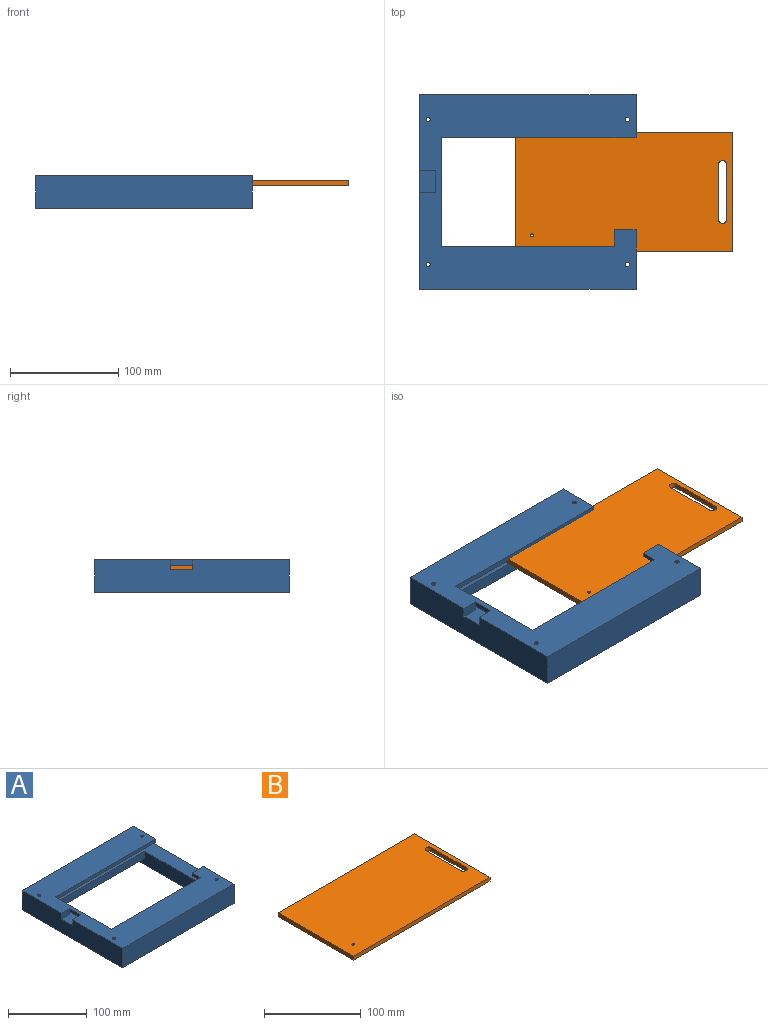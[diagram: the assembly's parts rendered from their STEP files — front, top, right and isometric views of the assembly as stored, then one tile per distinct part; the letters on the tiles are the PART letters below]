
ASSEMBLY  parts=2 mates=2
PART A: 32 faces, bbox 200x180x30 mm
  f0: plane 54.46x4mm, normal (1,0,0), area 217.8mm2, adj f3,f24,f25,f30
  f1: plane 200x180mm, normal (0,0,1), area 17949.7mm2, adj f2,f4,f5,f6,f7,f11,f12,f13
  f2: plane 180x30mm, normal (1,0,0), area 4535mm2, adj f1,f3,f4,f10,f11,f13,f24,f25
  f3: plane 185x110mm, normal (0,0,-1), area 2650mm2, adj f0,f2,f4,f5,f6,f7,f25,f26
  f4: plane 180x5mm, normal (0,-1,0), area 900mm2, adj f1,f2,f3,f6
  f5: plane 160x5mm, normal (0,1,0), area 800mm2, adj f1,f3,f6,f7
  f6: plane 100x5mm, normal (1,0,0), area 500mm2, adj f1,f3,f4,f5
  f7: plane 15x5mm, normal (-1,0,0), area 75mm2, adj f1,f3,f5,f28
  f8: plane 160x11mm, normal (0,-1,0), area 1760mm2, adj f14,f15,f23,f24
  f9: plane 160x11mm, normal (0,1,0), area 1760mm2, adj f14,f15,f20,f24
  f10: plane 200x180mm, normal (0,0,-1), area 10349.7mm2, adj f2,f11,f12,f13,f14,f15,f16,f17
  f11: plane 200x30mm, normal (0,1,0), area 6000mm2, adj f1,f2,f10,f12
  f12: plane 180x30mm, normal (-1,0,0), area 5220mm2, adj f1,f10,f11,f13,f24,f29,f30
  f13: plane 200x30mm, normal (0,-1,0), area 6000mm2, adj f1,f2,f10,f12
  f14: plane 160x21mm, normal (1,0,0), area 2700mm2, adj f8,f9,f10,f20,f21,f22,f23,f24
  f15: plane 160x21mm, normal (-1,0,0), area 2700mm2, adj f8,f9,f10,f20,f21,f22,f23,f24
  f16: cylinder r=2mm len=30mm, axis (0,0,1), area 377mm2, adj f1,f10
  f17: cylinder r=2mm len=30mm, axis (0,0,1), area 377mm2, adj f1,f10
  f18: cylinder r=2mm len=30mm, axis (0,0,1), area 377mm2, adj f1,f10
  f19: cylinder r=2mm len=30mm, axis (0,0,1), area 377mm2, adj f1,f10
  f20: plane 160x30mm, normal (0,0,-1), area 4800mm2, adj f9,f14,f15,f21
  f21: plane 160x10mm, normal (0,1,0), area 1600mm2, adj f10,f14,f15,f20
  f22: plane 160x10mm, normal (0,-1,0), area 1600mm2, adj f10,f14,f15,f23
  f23: plane 160x30mm, normal (0,0,-1), area 4800mm2, adj f8,f14,f15,f22
  f24: plane 200x110mm, normal (0,0,1), area 4650mm2, adj f0,f2,f8,f9,f12,f14,f15,f25
  f25: plane 185x4mm, normal (0,1,0), area 740mm2, adj f0,f2,f3,f24
  f26: plane 185x4mm, normal (0,-1,0), area 740mm2, adj f2,f3,f24,f27
  f27: plane 35.54x4mm, normal (1,0,0), area 142.2mm2, adj f3,f24,f26,f29
  f28: plane 20x5mm, normal (0,1,0), area 100mm2, adj f1,f2,f3,f7
  f29: plane 15x9mm, normal (0,-1,0), area 135mm2, adj f1,f12,f24,f27,f31
  f30: plane 15x9mm, normal (0,1,0), area 135mm2, adj f0,f1,f12,f24,f31
  f31: plane 20x5mm, normal (-1,0,0), area 100mm2, adj f1,f3,f29,f30
PART B: 11 faces, bbox 200x110x5 mm
  f0: plane 200x110mm, normal (0,0,1), area 21544mm2, adj f2,f3,f4,f5,f6,f7,f8,f9
  f1: plane 200x110mm, normal (0,0,-1), area 21544mm2, adj f2,f3,f4,f5,f6,f7,f8,f9
  f2: plane 200x5mm, normal (0,1,0), area 1000mm2, adj f0,f1,f3,f5
  f3: plane 110x5mm, normal (-1,0,0), area 550mm2, adj f0,f1,f2,f4
  f4: plane 200x5mm, normal (0,-1,0), area 1000mm2, adj f0,f1,f3,f5
  f5: plane 110x5mm, normal (1,0,0), area 550mm2, adj f0,f1,f2,f4
  f6: cylinder r=1.35mm len=5mm, axis (0,0,1), area 42.4mm2, adj f0,f1
  f7: cylinder r=4mm len=8mm, axis (0,0,1), area 62.8mm2, adj f0,f1,f8,f10
  f8: plane 50x5mm, normal (1,0,0), area 250mm2, adj f0,f1,f7,f9
  f9: cylinder r=4mm len=8mm, axis (0,0,1), area 62.8mm2, adj f0,f1,f8,f10
  f10: plane 50x5mm, normal (-1,0,0), area 250mm2, adj f0,f1,f7,f9
PLACE A t=(-47.75,72.39,50.89)mm
PLACE B t=(4.19,112.8,71.89)mm
MATE planar B.f1 <-> A.f24  axis (0,0,-1) through (49.56,101.01,71.89)mm
MATE planar B.f2 <-> A.f26  axis (0,1,0) through (51.44,156,74.39)mm
